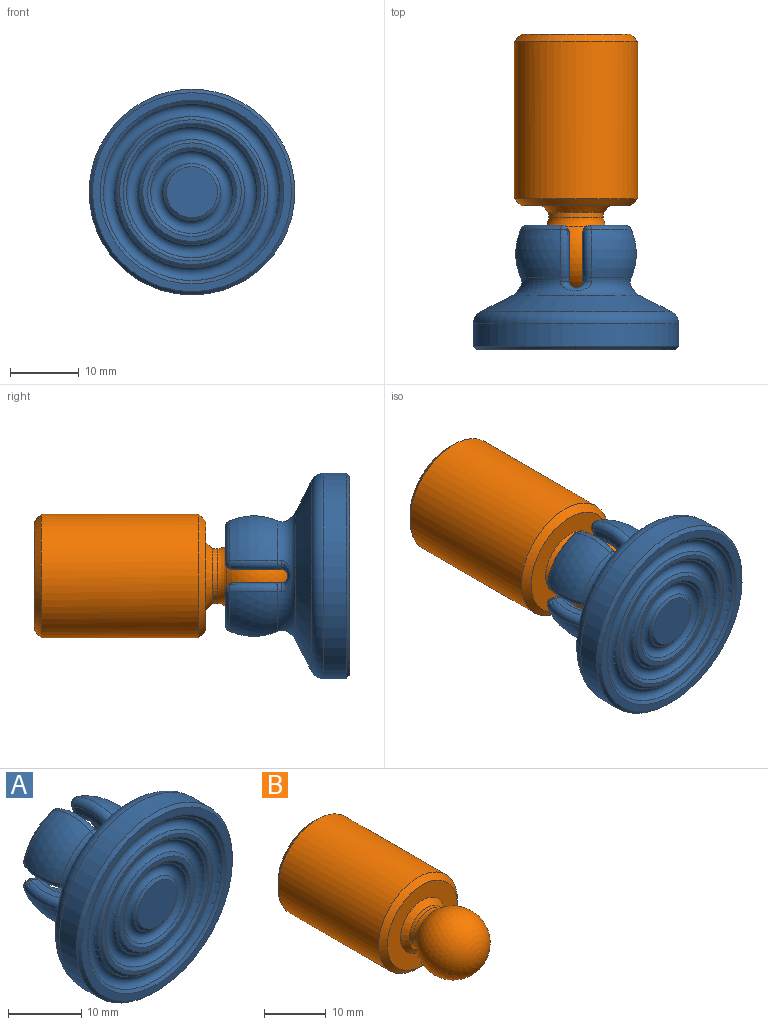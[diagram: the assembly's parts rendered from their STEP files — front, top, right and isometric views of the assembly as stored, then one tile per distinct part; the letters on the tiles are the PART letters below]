
ASSEMBLY  parts=2 mates=1
PART A: 93 faces, bbox 32.5x19.4x32.5 mm
  f0: plane 29x29mm, normal (0,-1,0), area 98.8mm2, adj f1,f81
  f1: cone r=15mm half-angle=45deg, axis (0,1,0), area 65.5mm2, adj f0,f2
  f2: cylinder r=15mm len=30mm, axis (0,1,0), area 308.6mm2, adj f1,f3
  f3: torus R=13mm, axis (0,1,0), area 202mm2, adj f2,f4
  f4: cone r=13.91mm half-angle=63deg, axis (0,-1,0), area 378.9mm2, adj f3,f5
  f5: torus R=10.18mm, axis (0,1,0), area 128.8mm2, adj f4,f6,f66,f67,f68,f69,f70,f71
  f6: sphere r=9.05mm, area 67.2mm2, adj f5,f7,f64,f65
  f7: torus R=7.8mm, axis (-1,0,0), area 12.8mm2, adj f6,f8,f62,f63,f80
  f8: plane 7.13x2.35mm, normal (1,0,0), area 7.5mm2, adj f7,f9,f60,f61,f80
  f9: cylinder r=1mm len=4.01mm, axis (0,0,-1), area 8.6mm2, adj f8,f10,f59,f79
  f10: plane 7.13x2.35mm, normal (-1,0,0), area 7.5mm2, adj f9,f11,f57,f58,f78
  f11: torus R=6.76mm, axis (1,0,0), area 8.8mm2, adj f10,f12,f57,f59
  f12: sphere r=6.05mm, area 223.3mm2, adj f11,f13,f38,f39,f40,f41,f42,f43
  f13: torus R=6.76mm, axis (-1,0,0), area 8.8mm2, adj f12,f14,f38,f56
  f14: plane 7.13x2.35mm, normal (1,0,0), area 7.5mm2, adj f13,f15,f29,f38,f70
  f15: cylinder r=1mm len=4.01mm, axis (0,0,1), area 8.6mm2, adj f14,f16,f56,f71
  f16: plane 7.13x2.35mm, normal (-1,0,0), area 7.5mm2, adj f15,f17,f54,f55,f72
  f17: torus R=7.8mm, axis (1,0,0), area 12.8mm2, adj f16,f18,f72,f73
  f18: sphere r=1mm, area 0.8mm2, adj f17,f19,f54
  f19: torus R=7.42mm, axis (0,1,0), area 13.4mm2, adj f18,f20,f53,f73
  f20: sphere r=1mm, area 1.3mm2, adj f19,f21,f52
  f21: torus R=7.8mm, axis (0,0,-1), area 12.8mm2, adj f20,f22,f73,f74
  f22: plane 7.13x2.35mm, normal (0,0,1), area 7.5mm2, adj f21,f23,f51,f52,f74
  f23: cylinder r=1mm len=4.01mm, axis (-1,0,0), area 8.6mm2, adj f22,f24,f50,f75
  f24: plane 7.13x2.35mm, normal (0,0,-1), area 7.5mm2, adj f23,f25,f48,f49,f76
  f25: torus R=7.8mm, axis (0,0,1), area 12.8mm2, adj f24,f26,f76,f77
  f26: sphere r=1mm, area 1.1mm2, adj f25,f27,f48
  f27: torus R=7.42mm, axis (0,1,0), area 13.4mm2, adj f26,f28,f47,f77
  f28: sphere r=1mm, area 2.1mm2, adj f27,f57,f58
  f29: torus R=7.8mm, axis (-1,0,0), area 12.8mm2, adj f14,f30,f69,f70
  f30: sphere r=1mm, area 1.3mm2, adj f29,f31,f38
  f31: torus R=7.42mm, axis (0,1,0), area 13.4mm2, adj f30,f32,f39,f69
  f32: sphere r=1mm, area 0.7mm2, adj f31,f33,f40
  f33: torus R=7.8mm, axis (0,0,-1), area 12.8mm2, adj f32,f34,f37,f68,f69
  f34: plane 7.13x2.35mm, normal (0,0,1), area 7.5mm2, adj f33,f35,f40,f41,f68
  f35: cylinder r=1mm len=4.01mm, axis (1,0,0), area 8.6mm2, adj f34,f36,f42,f67
  f36: plane 7.13x2.35mm, normal (0,0,-1), area 7.5mm2, adj f35,f43,f44,f64,f66
  f37: sphere r=1mm, area 0.1mm2, adj f33,f40
  f38: bspline ~4.99x3.37mm, area 2.3mm2, adj f12,f13,f14,f30,f39
  f39: cone r=5.24mm half-angle=60deg, axis (0,1,0), area 11.1mm2, adj f12,f31,f38,f40
  f40: bspline ~4.99x3.37mm, area 2.3mm2, adj f12,f32,f34,f37,f39,f41
  f41: torus R=6.76mm, axis (0,0,-1), area 8.8mm2, adj f12,f34,f40,f42
  f42: bspline ~3.44x2.67mm, area 4.6mm2, adj f12,f35,f41,f43
  f43: torus R=6.76mm, axis (0,0,1), area 8.8mm2, adj f12,f36,f42,f44
  f44: bspline ~4.99x3.37mm, area 2.3mm2, adj f12,f36,f43,f45,f46
  f45: sphere r=1mm, area 2.1mm2, adj f44,f64,f65
  f46: cone r=5.24mm half-angle=60deg, axis (0,1,0), area 11.1mm2, adj f12,f44,f60,f65
  f47: cone r=5.24mm half-angle=60deg, axis (0,1,0), area 11.1mm2, adj f12,f27,f48,f57
  f48: bspline ~4.99x3.37mm, area 2.3mm2, adj f12,f24,f26,f47,f49
  f49: torus R=6.76mm, axis (0,0,1), area 8.8mm2, adj f12,f24,f48,f50
  f50: bspline ~3.44x2.67mm, area 4.6mm2, adj f12,f23,f49,f51
  f51: torus R=6.76mm, axis (0,0,-1), area 8.8mm2, adj f12,f22,f50,f52
  f52: bspline ~4.99x3.37mm, area 2.3mm2, adj f12,f20,f22,f51,f53
  f53: cone r=5.24mm half-angle=60deg, axis (0,1,0), area 11.1mm2, adj f12,f19,f52,f54
  f54: bspline ~4.99x3.37mm, area 2.3mm2, adj f12,f16,f18,f53,f55
  f55: torus R=6.76mm, axis (1,0,0), area 8.8mm2, adj f12,f16,f54,f56
  f56: bspline ~3.44x2.67mm, area 4.6mm2, adj f12,f13,f15,f55
  f57: bspline ~4.99x3.37mm, area 2.3mm2, adj f10,f11,f12,f28,f47
  f58: torus R=7.8mm, axis (1,0,0), area 12.8mm2, adj f10,f28,f77,f78
  f59: bspline ~3.44x2.67mm, area 4.6mm2, adj f9,f11,f12,f61
  f60: bspline ~4.99x3.37mm, area 2.3mm2, adj f8,f12,f46,f61,f62,f63
  f61: torus R=6.76mm, axis (-1,0,0), area 8.8mm2, adj f8,f12,f59,f60
  f62: sphere r=1mm, area 0.1mm2, adj f7,f60
  f63: sphere r=1mm, area 0.8mm2, adj f7,f60,f65
  f64: torus R=7.8mm, axis (0,0,1), area 12.8mm2, adj f6,f36,f45,f66
  f65: torus R=7.42mm, axis (0,1,0), area 13.4mm2, adj f6,f45,f46,f63
  f66: bspline ~1.73x1.58mm, area 1.3mm2, adj f5,f36,f64,f67
  f67: bspline ~4.56x1.63mm, area 5.7mm2, adj f5,f35,f66,f68
  f68: bspline ~1.73x1.58mm, area 1.3mm2, adj f5,f33,f34,f67
  f69: sphere r=9.05mm, area 67.2mm2, adj f5,f29,f31,f33
  f70: bspline ~1.73x1.58mm, area 1.3mm2, adj f5,f14,f29,f71
  f71: bspline ~4.56x1.63mm, area 5.7mm2, adj f5,f15,f70,f72
  f72: bspline ~1.73x1.58mm, area 1.3mm2, adj f5,f16,f17,f71
  f73: sphere r=9.05mm, area 67.2mm2, adj f5,f17,f19,f21
  f74: bspline ~1.73x1.58mm, area 1.3mm2, adj f5,f21,f22,f75
  f75: bspline ~4.56x1.63mm, area 5.7mm2, adj f5,f23,f74,f76
  f76: bspline ~1.73x1.58mm, area 1.3mm2, adj f5,f24,f25,f75
  f77: sphere r=9.05mm, area 67.2mm2, adj f5,f25,f27,f58
  f78: bspline ~1.73x1.58mm, area 1.3mm2, adj f5,f10,f58,f79
  f79: bspline ~4.56x1.63mm, area 5.7mm2, adj f5,f9,f78,f80
  f80: bspline ~1.73x1.58mm, area 1.3mm2, adj f5,f7,f8,f79
  f81: cone r=12.9mm half-angle=55deg, axis (0,-1,0), area 47.3mm2, adj f0,f82
  f82: torus R=11.96mm, axis (0,-1,0), area 183.5mm2, adj f81,f83
  f83: cone r=11.02mm half-angle=55deg, axis (0,1,0), area 38.9mm2, adj f82,f84
  f84: plane 21.11x21.11mm, normal (0,-1,0), area 33.7mm2, adj f83,f85
  f85: cone r=9.56mm half-angle=54deg, axis (0,-1,0), area 36.2mm2, adj f84,f86
  f86: torus R=8.61mm, axis (0,-1,0), area 135.8mm2, adj f85,f87
  f87: cone r=7.66mm half-angle=54deg, axis (0,1,0), area 27.4mm2, adj f86,f88
  f88: plane 14.36x14.36mm, normal (0,-1,0), area 29.7mm2, adj f87,f89
  f89: cone r=6.03mm half-angle=56.1deg, axis (0,-1,0), area 22mm2, adj f88,f90
  f90: torus R=5.1mm, axis (0,-1,0), area 75.9mm2, adj f89,f91
  f91: cone r=4.17mm half-angle=56.1deg, axis (0,1,0), area 13.8mm2, adj f90,f92
  f92: plane 7.42x7.42mm, normal (0,-1,0), area 43.2mm2, adj f91
PART B: 18 faces, bbox 18x38.5x18 mm
  f0: cylinder r=5.12mm len=17.4mm, axis (0,1,0), area 223mm2, adj f6,f7,f10,f11,f15
  f1: plane 16x16mm, normal (0,1,0), area 83.2mm2, adj f6,f9
  f2: cylinder r=9mm len=23mm, axis (0,1,0), area 1300.6mm2, adj f8,f9
  f3: plane 16x16mm, normal (0,-1,0), area 122.5mm2, adj f8,f14
  f4: cylinder r=4mm len=8mm, axis (0,1,0), area 17.8mm2, adj f13,f14
  f5: sphere r=6mm, area 375.8mm2, adj f13
  f6: cone r=5.12mm half-angle=45deg, axis (0,1,0), area 34.1mm2, adj f0,f1,f7,f10,f11
  f7: cone r=5.12mm half-angle=45deg, axis (0,1,0), area 1.6mm2, adj f0,f6,f11
  f8: cone r=9mm half-angle=45deg, axis (0,1,0), area 75.5mm2, adj f2,f3
  f9: cone r=8mm half-angle=45deg, axis (0,-1,0), area 75.5mm2, adj f1,f2
  f10: bspline ~19.5x13.97mm, area 396.3mm2, adj f0,f6,f11,f12,f15
  f11: bspline ~19.77x13.97mm, area 412.3mm2, adj f0,f6,f7,f10,f12,f15
  f12: plane 0.78x0.57mm, normal (0,0,1), area 0.1mm2, adj f10,f11,f15
  f13: torus R=6mm, axis (0,-1,0), area 37.9mm2, adj f4,f5
  f14: cone r=5mm half-angle=45deg, axis (0,1,0), area 40mm2, adj f3,f4
  f15: cone r=6.1mm half-angle=45deg, axis (0,-1,0), area 37.2mm2, adj f0,f10,f11,f12,f16
  f16: cylinder r=6.1mm len=12.2mm, axis (0,-1,0), area 62.2mm2, adj f15,f17
  f17: plane 12.2x12.2mm, normal (0,1,0), area 116.9mm2, adj f16
PLACE A t=(0.13,4.93,-0.12)mm
PLACE B t=(0.13,36.93,-0.12)mm
MATE cylindrical B.f12 <-> A.f51  axis (0,0,1) through (0.13,4.93,-0.12)mm
